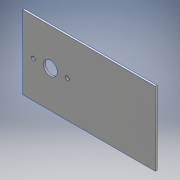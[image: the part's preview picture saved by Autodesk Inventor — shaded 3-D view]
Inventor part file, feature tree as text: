
AUTODESK INVENTOR PART (.ipt)
format: ipt  version: 2016 (Build 200138000, 138)  size: 125,952 bytes
history: native  units: mm
features: extrude x3, sketch x3, other x1
ambient origin geometry x8: Origin, YZ Plane, XZ Plane, XY Plane, X Axis, Y Axis, Z Axis, Center Point
bodies: Body1 (feature_tree)
feature tree (7):
  other  "ソリッド1"
  extrude  "押し出し1"  Depth=140.0mm
  extrude  "押し出し2"  Depth=80.0mm
  extrude  "押し出し3"  Depth=2.0mm TaperAngle=0.0deg
  sketch  "スケッチ1"
  sketch  "スケッチ2"
  sketch  "スケッチ3"
